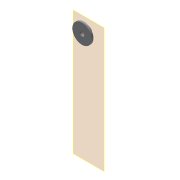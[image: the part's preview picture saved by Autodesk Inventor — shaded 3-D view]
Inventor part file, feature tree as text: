
AUTODESK INVENTOR PART (.ipt)
format: ipt  version: 2019.4 (Build 234330000, 330)  size: 91,648 bytes
history: native  units: mm
features: other x4, extrude x2, sketch x2, plane x1, reference x1
ambient origin geometry x8: Origin, YZ Plane, XZ Plane, XY Plane, X Axis, Y Axis, Z Axis, Center Point
bodies: Solid1 (feature_tree)
feature tree (10):
  plane  "Work Plane1"
  extrude  "Extrusion1"  Depth=5.1mm
  extrude  "Extrusion2"  Depth=2.0mm
  sketch  "Sketch1"  dims[d0=9.0mm d1=5.1mm]
  reference  "Reference1"
  sketch  "Sketch2"  dims[d2=5.0mm d3=0.0mm d4=22.0mm d5=2.0mm d6=0.0mm]
  other  "Assembly_Opentrons_Imagingunit_v3.iam"
  other  "Assembly_Opentrons_Autofocus_v2:1"
  other  "01_opticsmodule:1"
  other  "06_Fluorescence_Arm:1"
